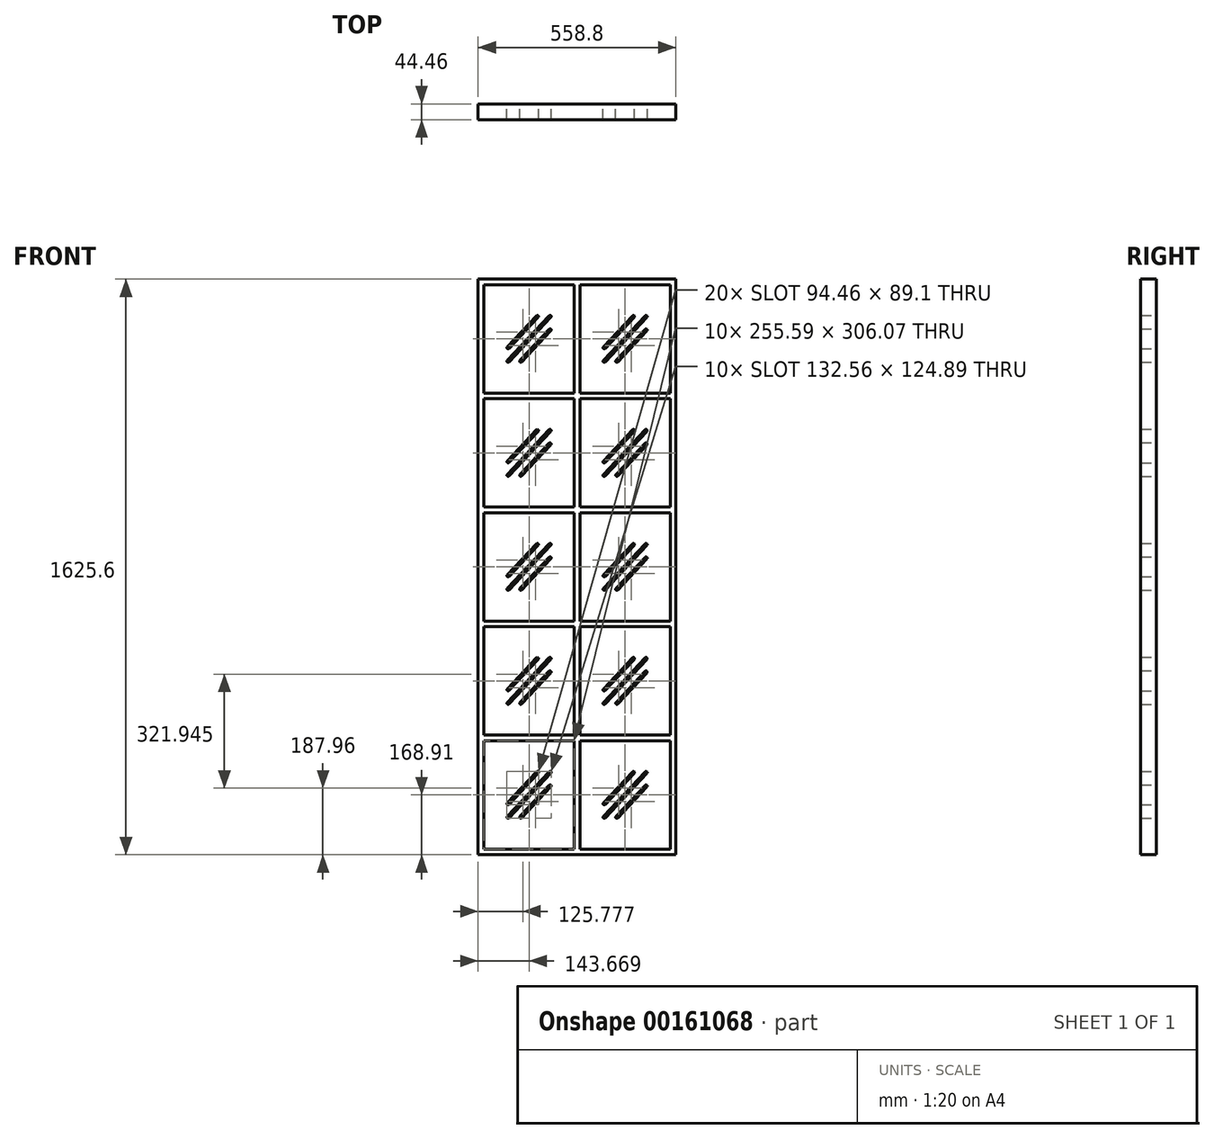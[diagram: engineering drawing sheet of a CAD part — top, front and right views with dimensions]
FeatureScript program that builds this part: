
annotation { "Feature Type Name" : "Feature", "Feature Type Description" : "" }
export const myFeature = defineFeature(function(context is Context, id is Id, definition is map)
    precondition{}
    {
        {
            var Q0;
            Q0=qCreatedBy(makeId("Front.planeOp"),FACE);
            var sketch = newSketch(context, id + "F0", { "sketchPlane" : qUnion([Q0])});
            skLineSegment(sketch, "E0.bottom", {"start": v(0, 0) * mm, "end": v(558.8, 0) * mm});
            skLineSegment(sketch, "E0.top", {"start": v(0, 1625.6) * mm, "end": v(558.8, 1625.6) * mm});
            skLineSegment(sketch, "E0.left", {"start": v(0, 0) * mm, "end": v(0, 1625.6) * mm});
            skLineSegment(sketch, "E0.right", {"start": v(558.8, 0) * mm, "end": v(558.8, 1625.6) * mm});
            skLineSegment(sketch, "E1.bottom", {"start": v(15.88, 15.88) * mm, "end": v(271.46, 15.88) * mm});
            skLineSegment(sketch, "E1.top", {"start": v(15.88, 321.95) * mm, "end": v(271.46, 321.95) * mm});
            skLineSegment(sketch, "E1.left", {"start": v(15.88, 15.88) * mm, "end": v(15.88, 321.95) * mm});
            skLineSegment(sketch, "E1.right", {"start": v(271.46, 15.88) * mm, "end": v(271.46, 321.95) * mm});
            skLineSegment(sketch, "E2.bottom", {"start": v(287.34, 15.88) * mm, "end": v(542.93, 15.88) * mm});
            skLineSegment(sketch, "E2.top", {"start": v(287.34, 321.95) * mm, "end": v(542.93, 321.95) * mm});
            skLineSegment(sketch, "E2.left", {"start": v(287.34, 15.88) * mm, "end": v(287.34, 321.95) * mm});
            skLineSegment(sketch, "E2.right", {"start": v(542.93, 15.88) * mm, "end": v(542.93, 321.95) * mm});
            skLineSegment(sketch, "E3.bottom", {"start": v(271.46, 337.82) * mm, "end": v(15.88, 337.82) * mm});
            skLineSegment(sketch, "E3.top", {"start": v(271.46, 643.9) * mm, "end": v(15.88, 643.9) * mm});
            skLineSegment(sketch, "E3.left", {"start": v(271.46, 337.82) * mm, "end": v(271.46, 643.9) * mm});
            skLineSegment(sketch, "E3.right", {"start": v(15.88, 337.82) * mm, "end": v(15.88, 643.9) * mm});
            skLineSegment(sketch, "E4.bottom", {"start": v(287.34, 337.82) * mm, "end": v(542.92, 337.82) * mm});
            skLineSegment(sketch, "E4.top", {"start": v(287.34, 643.9) * mm, "end": v(542.92, 643.9) * mm});
            skLineSegment(sketch, "E4.left", {"start": v(287.34, 337.82) * mm, "end": v(287.34, 643.9) * mm});
            skLineSegment(sketch, "E4.right", {"start": v(542.92, 337.82) * mm, "end": v(542.92, 643.9) * mm});
            skLineSegment(sketch, "E5.bottom", {"start": v(271.46, 659.77) * mm, "end": v(15.88, 659.77) * mm});
            skLineSegment(sketch, "E5.top", {"start": v(271.46, 965.84) * mm, "end": v(15.88, 965.84) * mm});
            skLineSegment(sketch, "E5.left", {"start": v(271.46, 659.77) * mm, "end": v(271.46, 965.84) * mm});
            skLineSegment(sketch, "E5.right", {"start": v(15.88, 659.77) * mm, "end": v(15.87, 965.84) * mm});
            skLineSegment(sketch, "E6.bottom", {"start": v(287.34, 659.77) * mm, "end": v(542.93, 659.77) * mm});
            skLineSegment(sketch, "E6.top", {"start": v(287.34, 965.84) * mm, "end": v(542.93, 965.84) * mm});
            skLineSegment(sketch, "E6.left", {"start": v(287.34, 659.77) * mm, "end": v(287.34, 965.84) * mm});
            skLineSegment(sketch, "E6.right", {"start": v(542.93, 659.77) * mm, "end": v(542.93, 965.84) * mm});
            skLineSegment(sketch, "E7.bottom", {"start": v(271.46, 981.7) * mm, "end": v(15.88, 981.7) * mm});
            skLineSegment(sketch, "E7.top", {"start": v(271.46, 1287.78) * mm, "end": v(15.87, 1287.78) * mm});
            skLineSegment(sketch, "E7.left", {"start": v(271.46, 981.7) * mm, "end": v(271.46, 1287.78) * mm});
            skLineSegment(sketch, "E7.right", {"start": v(15.88, 981.7) * mm, "end": v(15.87, 1287.78) * mm});
            skLineSegment(sketch, "E8.bottom", {"start": v(287.34, 981.7) * mm, "end": v(542.92, 981.7) * mm});
            skLineSegment(sketch, "E8.top", {"start": v(287.34, 1287.78) * mm, "end": v(542.92, 1287.78) * mm});
            skLineSegment(sketch, "E8.left", {"start": v(287.34, 981.7) * mm, "end": v(287.34, 1287.78) * mm});
            skLineSegment(sketch, "E8.right", {"start": v(542.92, 981.7) * mm, "end": v(542.92, 1287.78) * mm});
            skLineSegment(sketch, "E9.bottom", {"start": v(271.46, 1303.65) * mm, "end": v(15.87, 1303.65) * mm});
            skLineSegment(sketch, "E9.top", {"start": v(271.46, 1609.73) * mm, "end": v(15.87, 1609.73) * mm});
            skLineSegment(sketch, "E9.left", {"start": v(271.46, 1303.65) * mm, "end": v(271.46, 1609.73) * mm});
            skLineSegment(sketch, "E9.right", {"start": v(15.87, 1303.65) * mm, "end": v(15.87, 1609.73) * mm});
            skLineSegment(sketch, "E10.bottom", {"start": v(287.34, 1303.65) * mm, "end": v(542.92, 1303.65) * mm});
            skLineSegment(sketch, "E10.top", {"start": v(287.34, 1609.73) * mm, "end": v(542.93, 1609.73) * mm});
            skLineSegment(sketch, "E10.left", {"start": v(287.34, 1303.65) * mm, "end": v(287.34, 1609.73) * mm});
            skLineSegment(sketch, "E10.right", {"start": v(542.92, 1303.65) * mm, "end": v(542.92, 1609.73) * mm});
            skSolve(sketch);
        }
        {
            var Q0;
            Q0 = qSketchRegion(id + "F0", true);
            extrude(context, id + "F1", {"entities" : qUnion([Q0]), "depth" : 22.22 * mm, "hasSecondDirection" : true, "secondDirectionOppositeDirection" : true, "secondDirectionDepth" : 22.22 * mm});
        }
        {
            var Q0;
            Q0=qCreatedBy(makeId("Front.planeOp"),FACE);
            var sketch = newSketch(context, id + "F2", { "sketchPlane" : qUnion([Q0])});
            skLineSegment(sketch, "E11.0", {"start": v(271.46, 1609.73) * mm, "end": v(15.87, 1609.73) * mm});
            skLineSegment(sketch, "E12.0", {"start": v(15.87, 1303.65) * mm, "end": v(15.87, 1609.73) * mm});
            skLineSegment(sketch, "E13.0", {"start": v(271.46, 1303.65) * mm, "end": v(15.87, 1303.65) * mm});
            skLineSegment(sketch, "E14.0", {"start": v(287.34, 1303.65) * mm, "end": v(542.92, 1303.65) * mm});
            skLineSegment(sketch, "E15.0", {"start": v(287.34, 1303.65) * mm, "end": v(287.34, 1609.73) * mm});
            skLineSegment(sketch, "E16.0", {"start": v(287.34, 1609.73) * mm, "end": v(542.92, 1609.73) * mm});
            skLineSegment(sketch, "E17.0", {"start": v(542.92, 1303.65) * mm, "end": v(542.92, 1609.73) * mm});
            skLineSegment(sketch, "E18.0", {"start": v(287.34, 1287.78) * mm, "end": v(542.92, 1287.78) * mm});
            skLineSegment(sketch, "E19.0", {"start": v(542.92, 981.7) * mm, "end": v(542.92, 1287.78) * mm});
            skLineSegment(sketch, "E20.0", {"start": v(271.46, 1303.65) * mm, "end": v(271.46, 1609.73) * mm});
            skLineSegment(sketch, "E21.0", {"start": v(271.46, 981.7) * mm, "end": v(271.46, 1287.78) * mm});
            skLineSegment(sketch, "E22.0", {"start": v(287.34, 981.7) * mm, "end": v(542.92, 981.7) * mm});
            skLineSegment(sketch, "E23.0", {"start": v(287.34, 981.7) * mm, "end": v(287.34, 1287.78) * mm});
            skLineSegment(sketch, "E24.0", {"start": v(271.46, 1287.78) * mm, "end": v(15.87, 1287.78) * mm});
            skLineSegment(sketch, "E25.0", {"start": v(15.88, 981.7) * mm, "end": v(15.87, 1287.78) * mm});
            skLineSegment(sketch, "E26.0", {"start": v(271.46, 981.7) * mm, "end": v(15.88, 981.7) * mm});
            skLineSegment(sketch, "E27.0", {"start": v(271.46, 965.84) * mm, "end": v(15.88, 965.84) * mm});
            skLineSegment(sketch, "E28.0", {"start": v(15.88, 659.77) * mm, "end": v(15.87, 965.84) * mm});
            skLineSegment(sketch, "E29.0", {"start": v(271.46, 659.77) * mm, "end": v(271.46, 965.84) * mm});
            skLineSegment(sketch, "E30.0", {"start": v(271.46, 659.77) * mm, "end": v(15.88, 659.77) * mm});
            skLineSegment(sketch, "E31.0", {"start": v(287.34, 659.77) * mm, "end": v(287.34, 965.84) * mm});
            skLineSegment(sketch, "E32.0", {"start": v(287.34, 659.77) * mm, "end": v(542.93, 659.77) * mm});
            skLineSegment(sketch, "E33.0", {"start": v(542.93, 659.77) * mm, "end": v(542.93, 965.84) * mm});
            skLineSegment(sketch, "E34.0", {"start": v(287.34, 965.84) * mm, "end": v(542.93, 965.84) * mm});
            skLineSegment(sketch, "E35.0", {"start": v(287.34, 643.9) * mm, "end": v(542.92, 643.9) * mm});
            skLineSegment(sketch, "E36.0", {"start": v(542.92, 337.82) * mm, "end": v(542.92, 643.9) * mm});
            skLineSegment(sketch, "E37.0", {"start": v(287.34, 337.82) * mm, "end": v(542.92, 337.82) * mm});
            skLineSegment(sketch, "E38.0", {"start": v(287.34, 337.82) * mm, "end": v(287.34, 643.9) * mm});
            skLineSegment(sketch, "E39.0", {"start": v(271.46, 337.82) * mm, "end": v(271.46, 643.9) * mm});
            skLineSegment(sketch, "E40.0", {"start": v(271.46, 337.82) * mm, "end": v(15.88, 337.82) * mm});
            skLineSegment(sketch, "E41.0", {"start": v(271.46, 643.9) * mm, "end": v(15.88, 643.9) * mm});
            skLineSegment(sketch, "E42.0", {"start": v(15.88, 337.82) * mm, "end": v(15.88, 643.9) * mm});
            skLineSegment(sketch, "E43.0", {"start": v(15.88, 321.95) * mm, "end": v(271.46, 321.95) * mm});
            skLineSegment(sketch, "E44.0", {"start": v(15.88, 15.88) * mm, "end": v(15.88, 321.95) * mm});
            skLineSegment(sketch, "E45.0", {"start": v(271.46, 15.88) * mm, "end": v(271.46, 321.95) * mm});
            skLineSegment(sketch, "E46.0", {"start": v(15.88, 15.88) * mm, "end": v(271.46, 15.88) * mm});
            skLineSegment(sketch, "E47.0", {"start": v(287.34, 15.88) * mm, "end": v(287.34, 321.95) * mm});
            skLineSegment(sketch, "E48.0", {"start": v(287.34, 15.88) * mm, "end": v(542.93, 15.88) * mm});
            skLineSegment(sketch, "E49.0", {"start": v(542.93, 15.88) * mm, "end": v(542.93, 321.95) * mm});
            skLineSegment(sketch, "E50.0", {"start": v(287.34, 321.95) * mm, "end": v(542.93, 321.95) * mm});
            skLineSegment(sketch, "E51", {"start": v(202.94, 232.02) * mm, "end": v(84.4, 105.8) * mm});
            skLineSegment(sketch, "E52", {"start": v(202.94, 193.92) * mm, "end": v(120.18, 105.8) * mm});
            skLineSegment(sketch, "E53", {"start": v(167.16, 232.02) * mm, "end": v(84.4, 143.9) * mm});
            skArc(sketch, "E54.0.startCap", {"start": v(164.84, 234.19) * mm, "mid": v(169.33, 234.33) * mm, "end": v(169.47, 229.84) * mm});
            skArc(sketch, "E54.0.endCap", {"start": v(86.71, 141.73) * mm, "mid": v(82.22, 141.59) * mm, "end": v(82.08, 146.08) * mm});
            skLineSegment(sketch, "E54.0.left", {"start": v(169.47, 229.84) * mm, "end": v(86.71, 141.73) * mm});
            skLineSegment(sketch, "E54.0.right", {"start": v(164.84, 234.19) * mm, "end": v(82.08, 146.08) * mm});
            skArc(sketch, "E54.1.startCap", {"start": v(200.63, 234.19) * mm, "mid": v(205.11, 234.33) * mm, "end": v(205.25, 229.84) * mm});
            skArc(sketch, "E54.1.endCap", {"start": v(86.71, 103.63) * mm, "mid": v(82.22, 103.49) * mm, "end": v(82.08, 107.98) * mm});
            skLineSegment(sketch, "E54.1.left", {"start": v(205.25, 229.84) * mm, "end": v(86.71, 103.63) * mm});
            skLineSegment(sketch, "E54.1.right", {"start": v(200.63, 234.19) * mm, "end": v(82.08, 107.98) * mm});
            skArc(sketch, "E54.2.startCap", {"start": v(200.63, 196.09) * mm, "mid": v(205.11, 196.23) * mm, "end": v(205.25, 191.74) * mm});
            skArc(sketch, "E54.2.endCap", {"start": v(122.5, 103.63) * mm, "mid": v(118, 103.49) * mm, "end": v(117.87, 107.98) * mm});
            skLineSegment(sketch, "E54.2.left", {"start": v(205.25, 191.74) * mm, "end": v(122.5, 103.63) * mm});
            skLineSegment(sketch, "E54.2.right", {"start": v(200.63, 196.09) * mm, "end": v(117.87, 107.98) * mm});
            skLineSegment(sketch, "E55.0.1.0", {"start": v(202.94, 553.96) * mm, "end": v(84.4, 427.75) * mm});
            skLineSegment(sketch, "E55.0.1.1", {"start": v(200.63, 518.03) * mm, "end": v(117.87, 429.92) * mm});
            skLineSegment(sketch, "E55.0.1.2", {"start": v(205.25, 551.79) * mm, "end": v(86.71, 425.58) * mm});
            skLineSegment(sketch, "E55.0.1.3", {"start": v(164.84, 556.13) * mm, "end": v(82.08, 468.02) * mm});
            skLineSegment(sketch, "E55.0.1.4", {"start": v(205.25, 513.69) * mm, "end": v(122.5, 425.58) * mm});
            skLineSegment(sketch, "E55.0.1.5", {"start": v(169.47, 551.79) * mm, "end": v(86.71, 463.68) * mm});
            skLineSegment(sketch, "E55.0.1.6", {"start": v(202.94, 515.86) * mm, "end": v(120.18, 427.75) * mm});
            skLineSegment(sketch, "E55.0.1.7", {"start": v(167.16, 553.96) * mm, "end": v(84.4, 465.85) * mm});
            skLineSegment(sketch, "E55.0.1.8", {"start": v(200.63, 556.13) * mm, "end": v(82.08, 429.92) * mm});
            skArc(sketch, "E55.0.1.9", {"start": v(164.84, 556.13) * mm, "mid": v(169.33, 556.28) * mm, "end": v(169.47, 551.79) * mm});
            skArc(sketch, "E55.0.1.10", {"start": v(200.63, 556.13) * mm, "mid": v(205.11, 556.28) * mm, "end": v(205.25, 551.79) * mm});
            skArc(sketch, "E55.0.1.11", {"start": v(86.71, 425.58) * mm, "mid": v(82.22, 425.43) * mm, "end": v(82.08, 429.92) * mm});
            skArc(sketch, "E55.0.1.12", {"start": v(86.71, 463.68) * mm, "mid": v(82.22, 463.53) * mm, "end": v(82.08, 468.02) * mm});
            skArc(sketch, "E55.0.1.13", {"start": v(122.5, 425.58) * mm, "mid": v(118, 425.43) * mm, "end": v(117.87, 429.92) * mm});
            skArc(sketch, "E55.0.1.14", {"start": v(200.63, 518.03) * mm, "mid": v(205.11, 518.18) * mm, "end": v(205.25, 513.69) * mm});
            skLineSegment(sketch, "E55.0.2.0", {"start": v(202.94, 875.9) * mm, "end": v(84.4, 749.7) * mm});
            skLineSegment(sketch, "E55.0.2.1", {"start": v(200.63, 839.98) * mm, "end": v(117.87, 751.87) * mm});
            skLineSegment(sketch, "E55.0.2.2", {"start": v(205.25, 873.73) * mm, "end": v(86.71, 747.52) * mm});
            skLineSegment(sketch, "E55.0.2.3", {"start": v(164.84, 878.08) * mm, "end": v(82.08, 789.97) * mm});
            skLineSegment(sketch, "E55.0.2.4", {"start": v(205.25, 835.63) * mm, "end": v(122.5, 747.52) * mm});
            skLineSegment(sketch, "E55.0.2.5", {"start": v(169.47, 873.73) * mm, "end": v(86.71, 785.62) * mm});
            skLineSegment(sketch, "E55.0.2.6", {"start": v(202.94, 837.8) * mm, "end": v(120.18, 749.7) * mm});
            skLineSegment(sketch, "E55.0.2.7", {"start": v(167.16, 875.9) * mm, "end": v(84.4, 787.8) * mm});
            skLineSegment(sketch, "E55.0.2.8", {"start": v(200.63, 878.08) * mm, "end": v(82.08, 751.87) * mm});
            skArc(sketch, "E55.0.2.9", {"start": v(164.84, 878.08) * mm, "mid": v(169.33, 878.22) * mm, "end": v(169.47, 873.73) * mm});
            skArc(sketch, "E55.0.2.10", {"start": v(200.63, 878.08) * mm, "mid": v(205.11, 878.22) * mm, "end": v(205.25, 873.73) * mm});
            skArc(sketch, "E55.0.2.11", {"start": v(86.71, 747.52) * mm, "mid": v(82.22, 747.38) * mm, "end": v(82.08, 751.87) * mm});
            skArc(sketch, "E55.0.2.12", {"start": v(86.71, 785.62) * mm, "mid": v(82.22, 785.48) * mm, "end": v(82.08, 789.97) * mm});
            skArc(sketch, "E55.0.2.13", {"start": v(122.5, 747.52) * mm, "mid": v(118, 747.38) * mm, "end": v(117.87, 751.87) * mm});
            skArc(sketch, "E55.0.2.14", {"start": v(200.63, 839.98) * mm, "mid": v(205.11, 840.12) * mm, "end": v(205.25, 835.63) * mm});
            skLineSegment(sketch, "E55.0.3.0", {"start": v(202.94, 1197.85) * mm, "end": v(84.4, 1071.64) * mm});
            skLineSegment(sketch, "E55.0.3.1", {"start": v(200.63, 1161.92) * mm, "end": v(117.87, 1073.81) * mm});
            skLineSegment(sketch, "E55.0.3.2", {"start": v(205.25, 1195.68) * mm, "end": v(86.71, 1069.47) * mm});
            skLineSegment(sketch, "E55.0.3.3", {"start": v(164.84, 1200.02) * mm, "end": v(82.08, 1111.91) * mm});
            skLineSegment(sketch, "E55.0.3.4", {"start": v(205.25, 1157.58) * mm, "end": v(122.5, 1069.47) * mm});
            skLineSegment(sketch, "E55.0.3.5", {"start": v(169.47, 1195.68) * mm, "end": v(86.71, 1107.57) * mm});
            skLineSegment(sketch, "E55.0.3.6", {"start": v(202.94, 1159.75) * mm, "end": v(120.18, 1071.64) * mm});
            skLineSegment(sketch, "E55.0.3.7", {"start": v(167.16, 1197.85) * mm, "end": v(84.4, 1109.74) * mm});
            skLineSegment(sketch, "E55.0.3.8", {"start": v(200.63, 1200.02) * mm, "end": v(82.08, 1073.81) * mm});
            skArc(sketch, "E55.0.3.9", {"start": v(164.84, 1200.02) * mm, "mid": v(169.33, 1200.17) * mm, "end": v(169.47, 1195.68) * mm});
            skArc(sketch, "E55.0.3.10", {"start": v(200.63, 1200.02) * mm, "mid": v(205.11, 1200.17) * mm, "end": v(205.25, 1195.68) * mm});
            skArc(sketch, "E55.0.3.11", {"start": v(86.71, 1069.47) * mm, "mid": v(82.22, 1069.32) * mm, "end": v(82.08, 1073.81) * mm});
            skArc(sketch, "E55.0.3.12", {"start": v(86.71, 1107.57) * mm, "mid": v(82.22, 1107.42) * mm, "end": v(82.08, 1111.91) * mm});
            skArc(sketch, "E55.0.3.13", {"start": v(122.5, 1069.47) * mm, "mid": v(118, 1069.32) * mm, "end": v(117.87, 1073.81) * mm});
            skArc(sketch, "E55.0.3.14", {"start": v(200.63, 1161.92) * mm, "mid": v(205.11, 1162.07) * mm, "end": v(205.25, 1157.58) * mm});
            skLineSegment(sketch, "E55.0.4.0", {"start": v(202.94, 1519.8) * mm, "end": v(84.4, 1393.58) * mm});
            skLineSegment(sketch, "E55.0.4.1", {"start": v(200.63, 1483.87) * mm, "end": v(117.87, 1395.76) * mm});
            skLineSegment(sketch, "E55.0.4.2", {"start": v(205.25, 1517.62) * mm, "end": v(86.71, 1391.41) * mm});
            skLineSegment(sketch, "E55.0.4.3", {"start": v(164.84, 1521.97) * mm, "end": v(82.08, 1433.86) * mm});
            skLineSegment(sketch, "E55.0.4.4", {"start": v(205.25, 1479.52) * mm, "end": v(122.5, 1391.41) * mm});
            skLineSegment(sketch, "E55.0.4.5", {"start": v(169.47, 1517.62) * mm, "end": v(86.71, 1429.51) * mm});
            skLineSegment(sketch, "E55.0.4.6", {"start": v(202.94, 1481.7) * mm, "end": v(120.18, 1393.58) * mm});
            skLineSegment(sketch, "E55.0.4.7", {"start": v(167.16, 1519.8) * mm, "end": v(84.4, 1431.68) * mm});
            skLineSegment(sketch, "E55.0.4.8", {"start": v(200.63, 1521.97) * mm, "end": v(82.08, 1395.76) * mm});
            skArc(sketch, "E55.0.4.9", {"start": v(164.84, 1521.97) * mm, "mid": v(169.33, 1522.11) * mm, "end": v(169.47, 1517.62) * mm});
            skArc(sketch, "E55.0.4.10", {"start": v(200.63, 1521.97) * mm, "mid": v(205.11, 1522.11) * mm, "end": v(205.25, 1517.62) * mm});
            skArc(sketch, "E55.0.4.11", {"start": v(86.71, 1391.41) * mm, "mid": v(82.22, 1391.27) * mm, "end": v(82.08, 1395.76) * mm});
            skArc(sketch, "E55.0.4.12", {"start": v(86.71, 1429.51) * mm, "mid": v(82.22, 1429.37) * mm, "end": v(82.08, 1433.86) * mm});
            skArc(sketch, "E55.0.4.13", {"start": v(122.5, 1391.41) * mm, "mid": v(118, 1391.27) * mm, "end": v(117.87, 1395.76) * mm});
            skArc(sketch, "E55.0.4.14", {"start": v(200.63, 1483.87) * mm, "mid": v(205.11, 1484.01) * mm, "end": v(205.25, 1479.52) * mm});
            skLineSegment(sketch, "E55.1.0.0", {"start": v(474.4, 232.02) * mm, "end": v(355.86, 105.8) * mm});
            skLineSegment(sketch, "E55.1.0.1", {"start": v(472.09, 196.09) * mm, "end": v(389.33, 107.98) * mm});
            skLineSegment(sketch, "E55.1.0.2", {"start": v(476.72, 229.84) * mm, "end": v(358.17, 103.63) * mm});
            skLineSegment(sketch, "E55.1.0.3", {"start": v(436.3, 234.19) * mm, "end": v(353.55, 146.08) * mm});
            skLineSegment(sketch, "E55.1.0.4", {"start": v(476.72, 191.74) * mm, "end": v(393.96, 103.63) * mm});
            skLineSegment(sketch, "E55.1.0.5", {"start": v(440.93, 229.84) * mm, "end": v(358.17, 141.73) * mm});
            skLineSegment(sketch, "E55.1.0.6", {"start": v(474.4, 193.92) * mm, "end": v(391.64, 105.8) * mm});
            skLineSegment(sketch, "E55.1.0.7", {"start": v(438.62, 232.02) * mm, "end": v(355.86, 143.9) * mm});
            skLineSegment(sketch, "E55.1.0.8", {"start": v(472.09, 234.19) * mm, "end": v(353.55, 107.98) * mm});
            skArc(sketch, "E55.1.0.9", {"start": v(436.3, 234.19) * mm, "mid": v(440.8, 234.33) * mm, "end": v(440.93, 229.84) * mm});
            skArc(sketch, "E55.1.0.10", {"start": v(472.09, 234.19) * mm, "mid": v(476.58, 234.33) * mm, "end": v(476.72, 229.84) * mm});
            skArc(sketch, "E55.1.0.11", {"start": v(358.17, 103.63) * mm, "mid": v(353.69, 103.49) * mm, "end": v(353.55, 107.98) * mm});
            skArc(sketch, "E55.1.0.12", {"start": v(358.17, 141.73) * mm, "mid": v(353.69, 141.59) * mm, "end": v(353.55, 146.08) * mm});
            skArc(sketch, "E55.1.0.13", {"start": v(393.96, 103.63) * mm, "mid": v(389.47, 103.49) * mm, "end": v(389.33, 107.98) * mm});
            skArc(sketch, "E55.1.0.14", {"start": v(472.09, 196.09) * mm, "mid": v(476.58, 196.23) * mm, "end": v(476.72, 191.74) * mm});
            skLineSegment(sketch, "E55.1.1.0", {"start": v(474.4, 553.96) * mm, "end": v(355.86, 427.75) * mm});
            skLineSegment(sketch, "E55.1.1.1", {"start": v(472.09, 518.03) * mm, "end": v(389.33, 429.92) * mm});
            skLineSegment(sketch, "E55.1.1.2", {"start": v(476.72, 551.79) * mm, "end": v(358.17, 425.58) * mm});
            skLineSegment(sketch, "E55.1.1.3", {"start": v(436.3, 556.13) * mm, "end": v(353.55, 468.02) * mm});
            skLineSegment(sketch, "E55.1.1.4", {"start": v(476.72, 513.69) * mm, "end": v(393.96, 425.58) * mm});
            skLineSegment(sketch, "E55.1.1.5", {"start": v(440.93, 551.79) * mm, "end": v(358.17, 463.68) * mm});
            skLineSegment(sketch, "E55.1.1.6", {"start": v(474.4, 515.86) * mm, "end": v(391.64, 427.75) * mm});
            skLineSegment(sketch, "E55.1.1.7", {"start": v(438.62, 553.96) * mm, "end": v(355.86, 465.85) * mm});
            skLineSegment(sketch, "E55.1.1.8", {"start": v(472.09, 556.13) * mm, "end": v(353.55, 429.92) * mm});
            skArc(sketch, "E55.1.1.9", {"start": v(436.3, 556.13) * mm, "mid": v(440.8, 556.28) * mm, "end": v(440.93, 551.79) * mm});
            skArc(sketch, "E55.1.1.10", {"start": v(472.09, 556.13) * mm, "mid": v(476.58, 556.28) * mm, "end": v(476.72, 551.79) * mm});
            skArc(sketch, "E55.1.1.11", {"start": v(358.17, 425.58) * mm, "mid": v(353.69, 425.43) * mm, "end": v(353.55, 429.92) * mm});
            skArc(sketch, "E55.1.1.12", {"start": v(358.17, 463.68) * mm, "mid": v(353.69, 463.53) * mm, "end": v(353.55, 468.02) * mm});
            skArc(sketch, "E55.1.1.13", {"start": v(393.96, 425.58) * mm, "mid": v(389.47, 425.43) * mm, "end": v(389.33, 429.92) * mm});
            skArc(sketch, "E55.1.1.14", {"start": v(472.09, 518.03) * mm, "mid": v(476.58, 518.18) * mm, "end": v(476.72, 513.69) * mm});
            skLineSegment(sketch, "E55.1.2.0", {"start": v(474.4, 875.9) * mm, "end": v(355.86, 749.7) * mm});
            skLineSegment(sketch, "E55.1.2.1", {"start": v(472.09, 839.98) * mm, "end": v(389.33, 751.87) * mm});
            skLineSegment(sketch, "E55.1.2.2", {"start": v(476.72, 873.73) * mm, "end": v(358.17, 747.52) * mm});
            skLineSegment(sketch, "E55.1.2.3", {"start": v(436.3, 878.08) * mm, "end": v(353.55, 789.97) * mm});
            skLineSegment(sketch, "E55.1.2.4", {"start": v(476.72, 835.63) * mm, "end": v(393.96, 747.52) * mm});
            skLineSegment(sketch, "E55.1.2.5", {"start": v(440.93, 873.73) * mm, "end": v(358.17, 785.62) * mm});
            skLineSegment(sketch, "E55.1.2.6", {"start": v(474.4, 837.8) * mm, "end": v(391.64, 749.7) * mm});
            skLineSegment(sketch, "E55.1.2.7", {"start": v(438.62, 875.9) * mm, "end": v(355.86, 787.8) * mm});
            skLineSegment(sketch, "E55.1.2.8", {"start": v(472.09, 878.08) * mm, "end": v(353.55, 751.87) * mm});
            skArc(sketch, "E55.1.2.9", {"start": v(436.3, 878.08) * mm, "mid": v(440.8, 878.22) * mm, "end": v(440.93, 873.73) * mm});
            skArc(sketch, "E55.1.2.10", {"start": v(472.09, 878.08) * mm, "mid": v(476.58, 878.22) * mm, "end": v(476.72, 873.73) * mm});
            skArc(sketch, "E55.1.2.11", {"start": v(358.17, 747.52) * mm, "mid": v(353.69, 747.38) * mm, "end": v(353.55, 751.87) * mm});
            skArc(sketch, "E55.1.2.12", {"start": v(358.17, 785.62) * mm, "mid": v(353.69, 785.48) * mm, "end": v(353.55, 789.97) * mm});
            skArc(sketch, "E55.1.2.13", {"start": v(393.96, 747.52) * mm, "mid": v(389.47, 747.38) * mm, "end": v(389.33, 751.87) * mm});
            skArc(sketch, "E55.1.2.14", {"start": v(472.09, 839.98) * mm, "mid": v(476.58, 840.12) * mm, "end": v(476.72, 835.63) * mm});
            skLineSegment(sketch, "E55.1.3.0", {"start": v(474.4, 1197.85) * mm, "end": v(355.86, 1071.64) * mm});
            skLineSegment(sketch, "E55.1.3.1", {"start": v(472.09, 1161.92) * mm, "end": v(389.33, 1073.81) * mm});
            skLineSegment(sketch, "E55.1.3.2", {"start": v(476.72, 1195.68) * mm, "end": v(358.17, 1069.47) * mm});
            skLineSegment(sketch, "E55.1.3.3", {"start": v(436.3, 1200.02) * mm, "end": v(353.55, 1111.91) * mm});
            skLineSegment(sketch, "E55.1.3.4", {"start": v(476.72, 1157.58) * mm, "end": v(393.96, 1069.47) * mm});
            skLineSegment(sketch, "E55.1.3.5", {"start": v(440.93, 1195.68) * mm, "end": v(358.17, 1107.57) * mm});
            skLineSegment(sketch, "E55.1.3.6", {"start": v(474.4, 1159.75) * mm, "end": v(391.64, 1071.64) * mm});
            skLineSegment(sketch, "E55.1.3.7", {"start": v(438.62, 1197.85) * mm, "end": v(355.86, 1109.74) * mm});
            skLineSegment(sketch, "E55.1.3.8", {"start": v(472.09, 1200.02) * mm, "end": v(353.55, 1073.81) * mm});
            skArc(sketch, "E55.1.3.9", {"start": v(436.3, 1200.02) * mm, "mid": v(440.8, 1200.17) * mm, "end": v(440.93, 1195.68) * mm});
            skArc(sketch, "E55.1.3.10", {"start": v(472.09, 1200.02) * mm, "mid": v(476.58, 1200.17) * mm, "end": v(476.72, 1195.68) * mm});
            skArc(sketch, "E55.1.3.11", {"start": v(358.17, 1069.47) * mm, "mid": v(353.69, 1069.32) * mm, "end": v(353.55, 1073.81) * mm});
            skArc(sketch, "E55.1.3.12", {"start": v(358.17, 1107.57) * mm, "mid": v(353.69, 1107.42) * mm, "end": v(353.55, 1111.91) * mm});
            skArc(sketch, "E55.1.3.13", {"start": v(393.96, 1069.47) * mm, "mid": v(389.47, 1069.32) * mm, "end": v(389.33, 1073.81) * mm});
            skArc(sketch, "E55.1.3.14", {"start": v(472.09, 1161.92) * mm, "mid": v(476.58, 1162.07) * mm, "end": v(476.72, 1157.58) * mm});
            skLineSegment(sketch, "E55.1.4.0", {"start": v(474.4, 1519.8) * mm, "end": v(355.86, 1393.58) * mm});
            skLineSegment(sketch, "E55.1.4.1", {"start": v(472.09, 1483.87) * mm, "end": v(389.33, 1395.76) * mm});
            skLineSegment(sketch, "E55.1.4.2", {"start": v(476.72, 1517.62) * mm, "end": v(358.17, 1391.41) * mm});
            skLineSegment(sketch, "E55.1.4.3", {"start": v(436.3, 1521.97) * mm, "end": v(353.55, 1433.86) * mm});
            skLineSegment(sketch, "E55.1.4.4", {"start": v(476.72, 1479.52) * mm, "end": v(393.96, 1391.41) * mm});
            skLineSegment(sketch, "E55.1.4.5", {"start": v(440.93, 1517.62) * mm, "end": v(358.17, 1429.51) * mm});
            skLineSegment(sketch, "E55.1.4.6", {"start": v(474.4, 1481.7) * mm, "end": v(391.64, 1393.58) * mm});
            skLineSegment(sketch, "E55.1.4.7", {"start": v(438.62, 1519.8) * mm, "end": v(355.86, 1431.68) * mm});
            skLineSegment(sketch, "E55.1.4.8", {"start": v(472.09, 1521.97) * mm, "end": v(353.55, 1395.76) * mm});
            skArc(sketch, "E55.1.4.9", {"start": v(436.3, 1521.97) * mm, "mid": v(440.8, 1522.11) * mm, "end": v(440.93, 1517.62) * mm});
            skArc(sketch, "E55.1.4.10", {"start": v(472.09, 1521.97) * mm, "mid": v(476.58, 1522.11) * mm, "end": v(476.72, 1517.62) * mm});
            skArc(sketch, "E55.1.4.11", {"start": v(358.17, 1391.41) * mm, "mid": v(353.69, 1391.27) * mm, "end": v(353.55, 1395.76) * mm});
            skArc(sketch, "E55.1.4.12", {"start": v(358.17, 1429.51) * mm, "mid": v(353.69, 1429.37) * mm, "end": v(353.55, 1433.86) * mm});
            skArc(sketch, "E55.1.4.13", {"start": v(393.96, 1391.41) * mm, "mid": v(389.47, 1391.27) * mm, "end": v(389.33, 1395.76) * mm});
            skArc(sketch, "E55.1.4.14", {"start": v(472.09, 1483.87) * mm, "mid": v(476.58, 1484.01) * mm, "end": v(476.72, 1479.52) * mm});
            skLineSegment(sketch, "E55.direction1", {"start": v(82.08, 107.98) * mm, "end": v(353.55, 107.98) * mm, "construction": true});
            skLineSegment(sketch, "E55.direction2", {"start": v(82.08, 107.98) * mm, "end": v(82.08, 429.92) * mm, "construction": true});
            skSolve(sketch);
        }
        {
            var Q0;
            Q0 = qSketchRegion(id + "F2", true);
            extrude(context, id + "F3", {"entities" : qUnion([Q0]), "operationType" : NewBodyOperationType.ADD, "depth" : 21.59 * mm, "hasSecondDirection" : true, "secondDirectionOppositeDirection" : true, "secondDirectionDepth" : 21.59 * mm});
        }
    });
